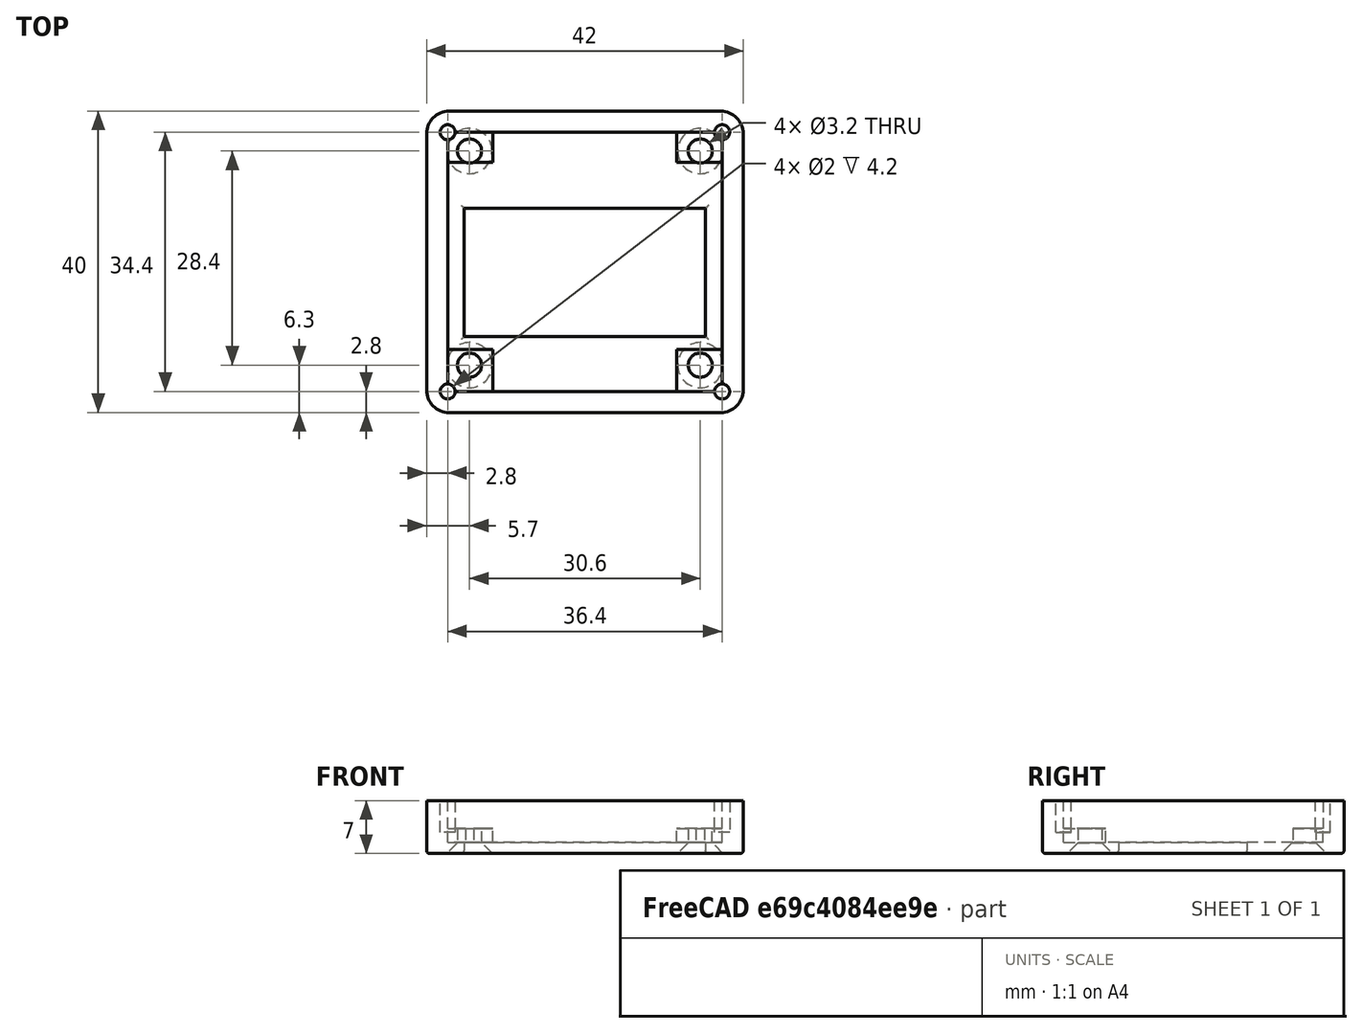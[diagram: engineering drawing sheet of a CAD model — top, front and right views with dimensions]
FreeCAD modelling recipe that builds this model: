
FCSTD DOCUMENT  (FreeCAD 0.18R16146 (Git))
Label: Bezel_OLED_13-KG-3
License: All rights reserved
LicenseURL: http://en.wikipedia.org/wiki/All_rights_reserved
objects: Sketcher::SketchObject×6, PartDesign::Pocket×4, PartDesign::Fillet×3, PartDesign::Pad×2, Spreadsheet::Sheet×1, PartDesign::Chamfer×1, PartDesign::Body×1, Mesh::Feature×1
note: 23 computed .brp shape members not serialized (recipe doc carries the construction recipe); baked Part::Feature solids carry a one-line shape summary decoded from their .brp

FEATURE [Sketcher::SketchObject] Sketch
  MapMode = 5
  Support = -> [XY_Plane]
  expr: Constraints[11] = Constraints.Laenge / 2
  expr: Constraints[10] = Constraints.Breite / 2
  expr: Constraints.Laenge = Measures.A2
  expr: Constraints.Breite = Measures.B2
  sketch-geometry (4):
    g0: LineSegment StartX=-21 StartY=20 StartZ=0 EndX=21 EndY=20 EndZ=0
    g1: LineSegment StartX=21 StartY=20 StartZ=0 EndX=21 EndY=-20 EndZ=0
    g2: LineSegment StartX=21 StartY=-20 StartZ=0 EndX=-21 EndY=-20 EndZ=0
    g3: LineSegment StartX=-21 StartY=-20 StartZ=0 EndX=-21 EndY=20 EndZ=0
  constraints (12):
    c: Coincident(g0,g1)
    c: Coincident(g1,g2)
    c: Coincident(g2,g3)
    c: Coincident(g3,g0)
    c: Horizontal(g0)
    c: Horizontal(g2)
    c: Vertical(g1)
    c: Vertical(g3)
    c: DistanceX(g2,g2) = 42  'Laenge'
    c: DistanceY(g3,g3) = 40  'Breite'
    c: Distance(g-1,g2) = 20
    c: Distance(g-1,g3) = 21
FEATURE [Spreadsheet::Sheet] Spreadsheet  label="Measures"
  cells = A1=Laenge; B1=Breite; C1=Hoehe; D1=OLED_Laenge; E1=OLED_Breite; F1=OLED_Tiefe; A2=42; B2=40; C2=7; D2=36.4; E2=34.4; F2=5.5
FEATURE [PartDesign::Pad] Pad
  Length = 7
  Length2 = 100
  Profile = -> Sketch
  Type = 0
  expr: Length = Measures.C2
FEATURE [Sketcher::SketchObject] Sketch001
  MapMode = 5
  Placement = pos=(0,0,7) rot=(0,0,1;0rad)
  Support = -> [Pad]
  expr: Constraints[11] = Constraints.OLED_Laenge / 2
  expr: Constraints[10] = Constraints.OLED_Breite / 2
  expr: Constraints.OLED_Laenge = Measures.D2
  expr: Constraints.OLED_Breite = Measures.E2
  sketch-geometry (4):
    g0: LineSegment StartX=-18.2 StartY=17.2 StartZ=0 EndX=18.2 EndY=17.2 EndZ=0
    g1: LineSegment StartX=18.2 StartY=17.2 StartZ=0 EndX=18.2 EndY=-17.2 EndZ=0
    g2: LineSegment StartX=18.2 StartY=-17.2 StartZ=0 EndX=-18.2 EndY=-17.2 EndZ=0
    g3: LineSegment StartX=-18.2 StartY=-17.2 StartZ=0 EndX=-18.2 EndY=17.2 EndZ=0
  constraints (12):
    c: Coincident(g0,g1)
    c: Coincident(g1,g2)
    c: Coincident(g2,g3)
    c: Coincident(g3,g0)
    c: Horizontal(g0)
    c: Horizontal(g2)
    c: Vertical(g1)
    c: Vertical(g3)
    c: DistanceY(g3,g3) = 34.4  'OLED_Breite'
    c: Distance(g2) = 36.4  'OLED_Laenge'
    c: Distance(g-1,g2) = 17.2
    c: Distance(g-1,g3) = 18.2
FEATURE [PartDesign::Pocket] Pocket
  BaseFeature = -> Pad
  Length = 5.5
  Length2 = 100
  Profile = -> Sketch001
  Type = 0
  expr: Length = Measures.F2
FEATURE [Sketcher::SketchObject] Sketch003
  MapMode = 5
  Placement = pos=(0,0,1.5) rot=(0,0,1;0rad)
  Support = -> [Pocket]
  sketch-geometry (4):
    g0: LineSegment StartX=-16 StartY=7.1 StartZ=0 EndX=16 EndY=7.1 EndZ=0
    g1: LineSegment StartX=16 StartY=7.1 StartZ=0 EndX=16 EndY=-9.9 EndZ=0
    g2: LineSegment StartX=16 StartY=-9.9 StartZ=0 EndX=-16 EndY=-9.9 EndZ=0
    g3: LineSegment StartX=-16 StartY=-9.9 StartZ=0 EndX=-16 EndY=7.1 EndZ=0
FEATURE [PartDesign::Pocket] Pocket001
  BaseFeature = -> Pocket
  Length = 5
  Length2 = 100
  Profile = -> Sketch003
  Type = 1
FEATURE [Sketcher::SketchObject] Sketch004
  MapMode = 5
  Placement = pos=(0,0,1.5) rot=(0,0,1;0rad)
  Support = -> [Pocket001]
  sketch-geometry (16):
    g0: LineSegment StartX=-12.2 StartY=13.2 StartZ=0 EndX=-18.2 EndY=13.2 EndZ=0
    g1: LineSegment StartX=-18.2 StartY=13.2 StartZ=0 EndX=-18.2 EndY=17.2 EndZ=0
    g2: LineSegment StartX=-18.2 StartY=17.2 StartZ=0 EndX=-12.2 EndY=17.2 EndZ=0
    g3: LineSegment StartX=-12.2 StartY=17.2 StartZ=0 EndX=-12.2 EndY=13.2 EndZ=0
    g4: LineSegment StartX=12.2 StartY=17.2 StartZ=0 EndX=18.2 EndY=17.2 EndZ=0
    g5: LineSegment StartX=18.2 StartY=17.2 StartZ=0 EndX=18.2 EndY=13.2 EndZ=0
    g6: LineSegment StartX=18.2 StartY=13.2 StartZ=0 EndX=12.2 EndY=13.2 EndZ=0
    g7: LineSegment StartX=12.2 StartY=13.2 StartZ=0 EndX=12.2 EndY=17.2 EndZ=0
    g8: LineSegment StartX=12.2 StartY=-11.6 StartZ=0 EndX=18.2 EndY=-11.6 EndZ=0
    g9: LineSegment StartX=18.2 StartY=-11.6 StartZ=0 EndX=18.2 EndY=-17.2 EndZ=0
    g10: LineSegment StartX=18.2 StartY=-17.2 StartZ=0 EndX=12.2 EndY=-17.2 EndZ=0
    g11: LineSegment StartX=12.2 StartY=-17.2 StartZ=0 EndX=12.2 EndY=-11.6 EndZ=0
    g12: LineSegment StartX=-18.2 StartY=-11.6 StartZ=0 EndX=-12.2 EndY=-11.6 EndZ=0
    g13: LineSegment StartX=-12.2 StartY=-11.6 StartZ=0 EndX=-12.2 EndY=-17.2 EndZ=0
    g14: LineSegment StartX=-12.2 StartY=-17.2 StartZ=0 EndX=-18.2 EndY=-17.2 EndZ=0
    g15: LineSegment StartX=-18.2 StartY=-17.2 StartZ=0 EndX=-18.2 EndY=-11.6 EndZ=0
  constraints (40):
    c: Coincident(g0,g1)
    c: Coincident(g1,g2)
    c: Coincident(g2,g3)
    c: Coincident(g3,g0)
    c: Horizontal(g0)
    c: Horizontal(g2)
    c: Vertical(g1)
    c: Vertical(g3)
    c: DistanceX(g0,g0) = 6
    c: DistanceY(g3,g3) = 4
    c: Coincident(g4,g5)
    c: Coincident(g5,g6)
    c: Coincident(g6,g7)
    c: Coincident(g7,g4)
    c: Horizontal(g4)
    c: Horizontal(g6)
    c: Vertical(g5)
    c: Vertical(g7)
    c: DistanceX(g6,g6) = 6
    c: DistanceY(g7,g7) = 4
    c: Coincident(g8,g9)
    c: Coincident(g9,g10)
    c: Coincident(g10,g11)
    c: Coincident(g11,g8)
    c: Horizontal(g8)
    c: Horizontal(g10)
    c: Vertical(g9)
    c: Vertical(g11)
    c: DistanceX(g8,g8) = 6
    c: DistanceY(g11,g11) = 5.6
    c: Coincident(g12,g13)
    c: Coincident(g13,g14)
    c: Coincident(g14,g15)
    c: Coincident(g15,g12)
    c: Horizontal(g12)
    c: Horizontal(g14)
    c: Vertical(g13)
    c: Vertical(g15)
    c: DistanceY(g13,g13) = 5.6
    c: DistanceX(g12,g12) = 6
FEATURE [PartDesign::Pad] Pad001
  BaseFeature = -> Pocket001
  Length = 1.8
  Length2 = 100
  Profile = -> Sketch004
  Type = 0
FEATURE [Sketcher::SketchObject] Sketch005
  ExternalGeometry = -> [Pad001]
  MapMode = 5
  Placement = pos=(0,0,0) rot=(1,0,0;3.14159rad)
  Support = -> [Pad001]
  sketch-geometry (4):
    g0: Circle CenterX=15.3 CenterY=13.7 CenterZ=0 NormalX=0 NormalY=0 NormalZ=1 AngleXU=0 Radius=1.6
    g1: Circle CenterX=-15.3 CenterY=13.7 CenterZ=0 NormalX=0 NormalY=0 NormalZ=1 AngleXU=0 Radius=1.6
    g2: Circle CenterX=-15.3 CenterY=-14.7 CenterZ=0 NormalX=0 NormalY=0 NormalZ=1 AngleXU=0 Radius=1.6
    g3: Circle CenterX=15.3 CenterY=-14.7 CenterZ=0 NormalX=0 NormalY=0 NormalZ=1 AngleXU=0 Radius=1.6
  constraints (12):
    c: Radius(g0) = 1.6
    c: Equal(g0,g3)
    c: Equal(g0,g2)
    c: Equal(g0,g1)
    c: Distance(g1,g-5) = 6.3
    c: Distance(g0,g-5) = 6.3
    c: Distance(g3,g-5) = 34.7
    c: Distance(g2,g-5) = 34.7
    c: Distance(g3,g-4) = 5.7
    c: Distance(g0,g-4) = 5.7
    c: Distance(g1,g-3) = 5.7
    c: Distance(g2,g-3) = 5.7
FEATURE [PartDesign::Pocket] Pocket002
  BaseFeature = -> Pad001
  Length = 5
  Length2 = 100
  Profile = -> Sketch005
  Type = 1
FEATURE [Sketcher::SketchObject] Sketch006
  ExternalGeometry = -> [Pocket002]
  MapMode = 5
  Placement = pos=(0,0,7) rot=(0,0,1;0rad)
  Support = -> [Pocket002]
  sketch-geometry (4):
    g0: Circle CenterX=18.2 CenterY=17.2 CenterZ=0 NormalX=0 NormalY=0 NormalZ=1 AngleXU=0 Radius=1
    g1: Circle CenterX=-18.2 CenterY=17.2 CenterZ=0 NormalX=0 NormalY=0 NormalZ=1 AngleXU=0 Radius=1
    g2: Circle CenterX=-18.2 CenterY=-17.2 CenterZ=0 NormalX=0 NormalY=0 NormalZ=1 AngleXU=0 Radius=1
    g3: Circle CenterX=18.2 CenterY=-17.2 CenterZ=0 NormalX=0 NormalY=0 NormalZ=1 AngleXU=0 Radius=1
  constraints (8):
    c: Coincident(g0,g-3)
    c: Coincident(g1,g-4)
    c: Coincident(g2,g-4)
    c: Coincident(g3,g-3)
    c: Radius(g1) = 1
    c: Equal(g1,g0)
    c: Equal(g1,g3)
    c: Equal(g1,g2)
FEATURE [PartDesign::Pocket] Pocket003
  BaseFeature = -> Pocket002
  Length = 4.2
  Length2 = 100
  Profile = -> Sketch006
  Type = 0
FEATURE [PartDesign::Fillet] Fillet
  Base = -> Pocket003 [Edge5,Edge1,Edge2,Edge8]
  BaseFeature = -> Pocket003
  Radius = 3
FEATURE [PartDesign::Chamfer] Chamfer
  Base = -> Fillet [Edge12,Edge13,Edge14,Edge15]
  BaseFeature = -> Fillet
  Size = 1.4
FEATURE [PartDesign::Fillet] Fillet001
  Base = -> Chamfer [Edge11,Edge10,Edge12,Edge13]
  BaseFeature = -> Chamfer
  Radius = 0.4
FEATURE [PartDesign::Fillet] Fillet002
  Base = -> Fillet001 [Edge13,Edge12,Edge10,Edge8,Edge6,Edge7,Edge9,Edge11]
  BaseFeature = -> Fillet001
  Radius = 0.4
FEATURE [PartDesign::Body] Body
  Group = -> [Sketch,Pad,Sketch001,Pocket,Sketch003,Sketch004,Pocket001,Pad001,Sketch005,Pocket002,Sketch006,Pocket003,Fillet,Chamfer,Fillet001,Fillet002]
  Origin = -> Origin
  Tip = -> Fillet002
FEATURE [Mesh::Feature] Mesh  label="Fillet002 (Meshed)"
